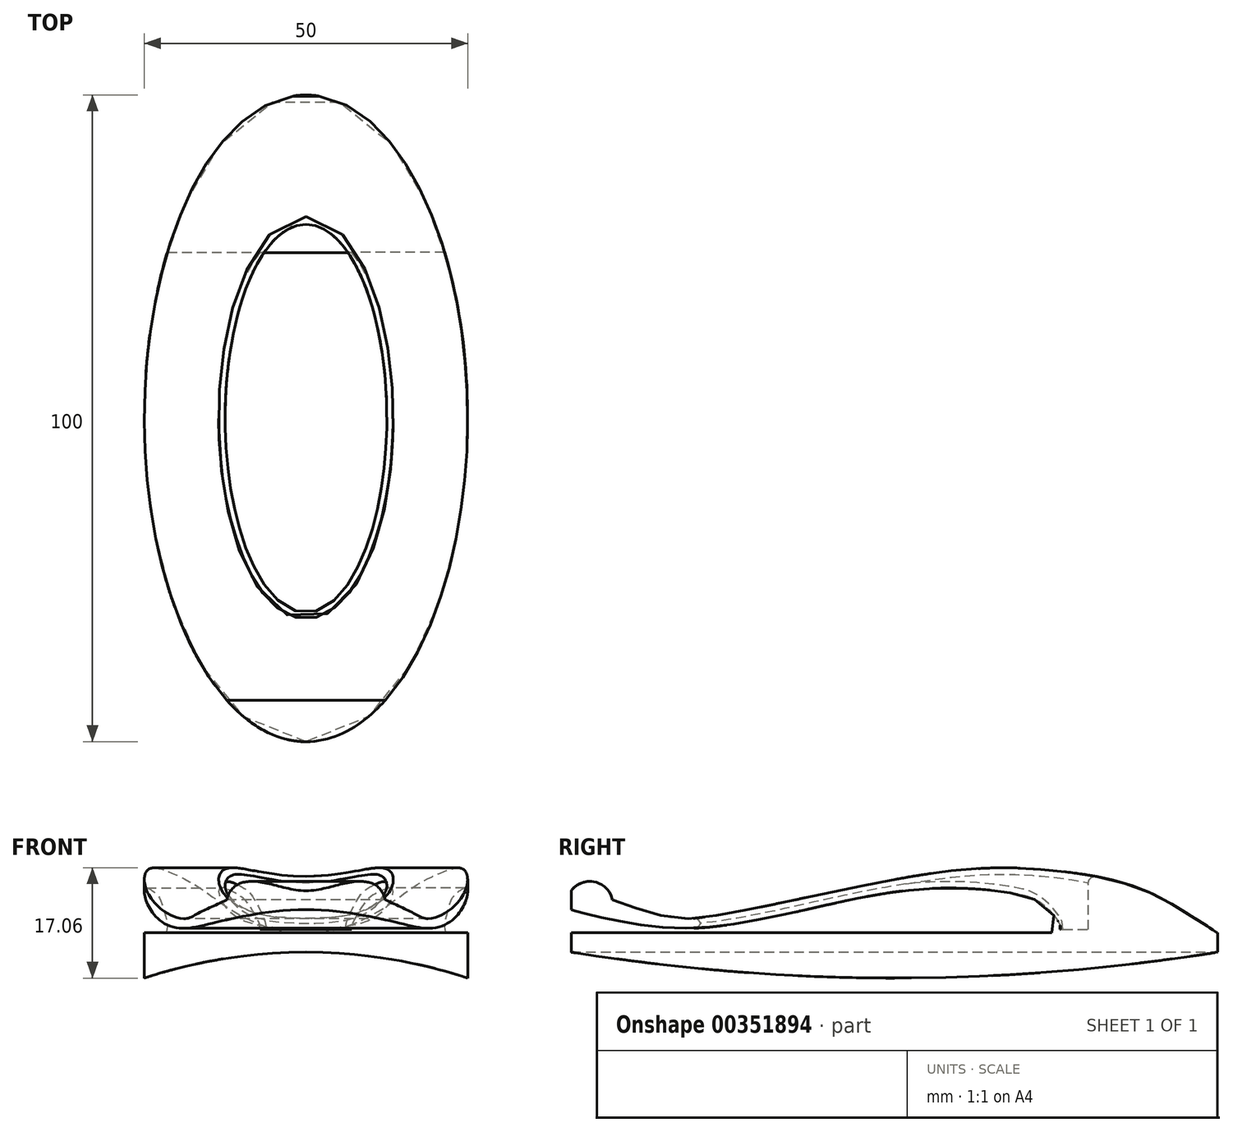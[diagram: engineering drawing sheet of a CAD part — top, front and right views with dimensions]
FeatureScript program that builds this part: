
annotation { "Feature Type Name" : "Feature", "Feature Type Description" : "" }
export const myFeature = defineFeature(function(context is Context, id is Id, definition is map)
    precondition{}
    {
        {
            assignVariable(context, id + "F0", {"name" : "baseWidth", "anyValue" : 50});
        }
        {
            var Q0;
            Q0=qCreatedBy(makeId("Top.planeOp"),FACE);
            var sketch = newSketch(context, id + "F1", { "sketchPlane" : qUnion([Q0])});
            skLineSegment(sketch, "E0.bottom", {"start": v(-25, 50) * mm, "end": v(25, 50) * mm});
            skLineSegment(sketch, "E0.top", {"start": v(-25, -50) * mm, "end": v(25, -50) * mm});
            skLineSegment(sketch, "E0.left", {"start": v(-25, 50) * mm, "end": v(-25, -50) * mm});
            skLineSegment(sketch, "E0.right", {"start": v(25, 50) * mm, "end": v(25, -50) * mm});
            skPoint(sketch, "E0.middle", {"position": v(0, 0) * mm});
            skSolve(sketch);
        }
        {
            var Q0;
            Q0 = qSketchRegion(id + "F1", true);
            extrude(context, id + "F2", {"entities" : qUnion([Q0]), "oppositeDirection" : true, "depth" : 9 * mm});
        }
        {
            var Q0;
            Q0=qCreatedBy(makeId("Front.planeOp"),FACE);
            var sketch = newSketch(context, id + "F3", { "sketchPlane" : qUnion([Q0])});
            skLineSegment(sketch, "E1", {"start": v(0, 0) * mm, "end": v(0, -3) * mm, "construction": true});
            skLineSegment(sketch, "E2", {"start": v(0, -3) * mm, "end": v(0, -83) * mm, "construction": true});
            skPoint(sketch, "E3.MirrorCS.end.orphan", {"position": v(27.63, -4.62) * mm});
            skPoint(sketch, "E3.MirrorCS.start.orphan", {"position": v(0, 0) * mm});
            skPoint(sketch, "E4.MirrorCS.end.orphan", {"position": v(25.3, -9.1) * mm});
            skPoint(sketch, "E5.start.orphan", {"position": v(-27.63, -4.62) * mm});
            skPoint(sketch, "E6.end.orphan", {"position": v(-25.3, -9.1) * mm});
            skPoint(sketch, "E7.MirrorCS.start.orphan", {"position": v(0, -3) * mm});
            skCircle(sketch, "E8", {"center": v(0, -83) * mm, "radius": 80 * mm});
            skSolve(sketch);
        }
        {
            var Q0;
            Q0 = qSketchRegion(id + "F3", true);
            extrude(context, id + "F4", {"entities" : qUnion([Q0]), "operationType" : NewBodyOperationType.REMOVE, "depth" : 58.6 * mm, "hasSecondDirection" : true, "secondDirectionOppositeDirection" : true, "secondDirectionDepth" : 93.1 * mm});
        }
        {
            var Q0;
            Q0=qSketchRegion(id+"F3",true);
            extrude(context, id + "F5", {"entities" : qUnion([Q0]), "operationType" : NewBodyOperationType.REMOVE, "depth" : 59.3 * mm, "hasSecondDirection" : true, "secondDirectionOppositeDirection" : true, "secondDirectionDepth" : 67.2 * mm});
        }
        {
            var Q0;
            Q0=qCreatedBy(makeId("Right.planeOp"),FACE);
            var sketch = newSketch(context, id + "F6", { "sketchPlane" : qUnion([Q0])});
            skLineSegment(sketch, "E9", {"start": v(0, 0) * mm, "end": v(70.45, 0) * mm, "construction": true});
            skFitSpline(sketch, "E10", {"points": [v(49.84, 0) * mm, v(45.5, 2.82) * mm, v(37.77, 6.91) * mm, v(25.1, 9.58) * mm, v(4.82, 9.05) * mm, v(-31.53, 2.2) * mm, v(-37.07, 2.96) * mm, v(-43.6, 5.1) * mm], "startDerivative": vector(-43.63, 31.79) * mm, "endDerivative": vector(-64.7, 27.4) * mm});
            skFitSpline(sketch, "E11", {"points": [v(24.33, 0) * mm, v(23.88, 3.52) * mm, v(18.73, 6.05) * mm, v(7.22, 6.9) * mm, v(-8.3, 4.78) * mm, v(-30.23, 0.75) * mm, v(-42.88, 1.88) * mm, v(-50.65, 3.78) * mm], "startDerivative": vector(92.2, 0) * mm, "endDerivative": vector(-63.45, 20.53) * mm});
            skArc(sketch, "E12", {"start": v(-43.6, 5.1) * mm, "mid": v(-47.78, 7.89) * mm, "end": v(-50.65, 3.78) * mm});
            skPoint(sketch, "E12.third.point", {"position": v(-49.52, 7.02) * mm});
            skArc(sketch, "E13", {"start": v(24.33, 0) * mm, "mid": v(37.09, -2.93) * mm, "end": v(49.84, 0) * mm});
            skSolve(sketch);
        }
        {
            var Q0;
            {var subQ1=sQuery(id+"F6.wireOp",EDGE,"E10");Q0=makeQuery(id+"F6.imprint","IMPRINT",FACE,{"disambiguationData":[TD([[makeQuery(id+"F6.imprint","IMPRINT",EDGE,{"derivedFrom":subQ1}),1.0]])]});}
            extrude(context, id + "F7", {"entities" : qUnion([Q0]), "depth" : (getVariable(context, 'baseWidth') / 2) * mm, "hasSecondDirection" : true, "secondDirectionOppositeDirection" : true, "secondDirectionDepth" : (getVariable(context, 'baseWidth') / 2) * mm});
        }
        {
            var Q0;
            Q0=qCreatedBy(makeId("Top.planeOp"),FACE);
            var sketch = newSketch(context, id + "F8", { "sketchPlane" : qUnion([Q0])});
            skEllipse(sketch, "E14", {"center": v(0, 0) * mm, "majorRadius": 30 * mm, "minorRadius": 12.5 * mm, "majorAxis": v(0, 1)});
            skSolve(sketch);
        }
        {
            var Q0;
            Q0=qSketchRegion(id+"F8",true);
            extrude(context, id + "F9", {"entities" : qUnion([Q0]), "operationType" : NewBodyOperationType.REMOVE, "depth" : 23.9 * mm, "hasSecondDirection" : true, "secondDirectionOppositeDirection" : false, "secondDirectionDepth" : 0.5 * mm});
        }
        {
            var Q0;
            Q0=qCreatedBy(makeId("Top.planeOp"),FACE);
            var sketch = newSketch(context, id + "F10", { "sketchPlane" : qUnion([Q0])});
            skEllipse(sketch, "E15", {"center": v(0, 0) * mm, "majorRadius": 50 * mm, "minorRadius": 25 * mm, "majorAxis": v(0, -1)});
            skSolve(sketch);
        }
        {
            var Q0;
            Q0 = qSketchRegion(id + "F10", true);
            extrude(context, id + "F11", {"entities" : qUnion([Q0]), "operationType" : NewBodyOperationType.INTERSECT, "oppositeDirection" : true, "depth" : 25 * mm, "hasSecondDirection" : true, "secondDirectionOppositeDirection" : false, "secondDirectionDepth" : 25 * mm});
        }
        {
            var Q0;
            Q0=makeQuery(id+"F2.opExtrude","SWEPT_BODY",BODY,{"disambiguationData":[OSD([sQuery(id+"F1.wireOp",EDGE,"E0.bottom"),sQuery(id+"F1.wireOp",EDGE,"E0.top"),sQuery(id+"F1.wireOp",EDGE,"E0.left"),sQuery(id+"F1.wireOp",EDGE,"E0.right")])]});
            var Q1;
            Q1=makeQuery(id+"F7.opExtrude","SWEPT_BODY",BODY,{"disambiguationData":[OSD([sQuery(id+"F6.wireOp",EDGE,"E10"),sQuery(id+"F6.wireOp",EDGE,"E11"),sQuery(id+"F6.wireOp",EDGE,"E12"),sQuery(id+"F6.wireOp",EDGE,"E13")])]});
            booleanBodies(context, id + "F12", {"operationType" : BooleanOperationType.UNION, "tools" : qUnion([Q0, Q1])});
        }
        {
            var Q0;
            Q0=makeQuery(id+"F11.boolean.opBoolean","INTERSECT",EDGE,{"disambiguationData":[OD(1.0)],"derivedFrom":[makeQuery(id+"F7.opExtrude","SWEPT_FACE",FACE,{"disambiguationData":[OSD([sQuery(id+"F6.wireOp",EDGE,"E10")])]}),makeQuery(id+"F11.boolean.toolComplement.opBoolean","COPY",FACE,{"derivedFrom":makeQuery(id+"F11.opExtrude","SWEPT_FACE",FACE,{"disambiguationData":[OSD([sQuery(id+"F10.wireOp",EDGE,"E15")])]})})]});
            var Q1;
            Q1=makeQuery(id+"F9.boolean.opBoolean","INTERSECT",EDGE,{"derivedFrom":[makeQuery(id+"F7.opExtrude","SWEPT_FACE",FACE,{"disambiguationData":[OSD([sQuery(id+"F6.wireOp",EDGE,"E10")])]}),makeQuery(id+"F9.opExtrude","SWEPT_FACE",FACE,{"disambiguationData":[OSD([sQuery(id+"F8.wireOp",EDGE,"E14")])]})]});
            var Q2;
            Q2=makeQuery(id+"F11.boolean.opBoolean","INTERSECT",EDGE,{"derivedFrom":[makeQuery(id+"F7.opExtrude","SWEPT_FACE",FACE,{"disambiguationData":[OSD([sQuery(id+"F6.wireOp",EDGE,"E12")])]}),makeQuery(id+"F11.boolean.toolComplement.opBoolean","COPY",FACE,{"derivedFrom":makeQuery(id+"F11.opExtrude","SWEPT_FACE",FACE,{"disambiguationData":[OSD([sQuery(id+"F10.wireOp",EDGE,"E15")])]})})]});
            var Q3;
            {var subQ0=sQuery(id+"F1.wireOp",EDGE,"E0.right");var subQ1=sQuery(id+"F1.wireOp",EDGE,"E0.left");var subQ2=sQuery(id+"F1.wireOp",EDGE,"E0.top");var subQ3=sQuery(id+"F1.wireOp",EDGE,"E0.bottom");var subQ4=makeQuery(id+"F2.opExtrude","CAP_FACE",FACE,{"disambiguationData":[OSD([subQ3,subQ2,subQ1,subQ0])],"isStart":true});var subQ5=makeQuery(id+"F7.opExtrude","SWEPT_FACE",FACE,{"disambiguationData":[OSD([sQuery(id+"F6.wireOp",EDGE,"E11")])]});var subQ6=makeQuery(id+"F11.boolean.toolComplement.opBoolean","COPY",FACE,{"derivedFrom":makeQuery(id+"F11.opExtrude","SWEPT_FACE",FACE,{"disambiguationData":[OSD([sQuery(id+"F10.wireOp",EDGE,"E15")])]})});Q3=makeQuery(id+"F12.opBoolean","SPLIT",EDGE,{"disambiguationData":[TD([subQ5])],"derivedFrom":makeQuery(id+"F11.boolean.opBoolean","INTERSECT",EDGE,{"derivedFrom":[subQ4,subQ6]})});}
            var Q4;
            Q4=makeQuery(id+"F9.boolean.opBoolean","INTERSECT",EDGE,{"derivedFrom":[makeQuery(id+"F7.opExtrude","SWEPT_FACE",FACE,{"disambiguationData":[OSD([sQuery(id+"F6.wireOp",EDGE,"E11")])]}),makeQuery(id+"F9.opExtrude","SWEPT_FACE",FACE,{"disambiguationData":[OSD([sQuery(id+"F8.wireOp",EDGE,"E14")])]})]});
            var Q5;
            Q5=makeQuery(id+"F11.boolean.opBoolean","INTERSECT",EDGE,{"derivedFrom":[makeQuery(id+"F4.boolean.opBoolean","COPY",FACE,{"derivedFrom":makeQuery(id+"F4.opExtrude","SWEPT_FACE",FACE,{"disambiguationData":[OSD([sQuery(id+"F3.wireOp",EDGE,"E8")])]})}),makeQuery(id+"F11.boolean.toolComplement.opBoolean","COPY",FACE,{"derivedFrom":makeQuery(id+"F11.opExtrude","SWEPT_FACE",FACE,{"disambiguationData":[OSD([sQuery(id+"F10.wireOp",EDGE,"E15")])]})})]});
            fillet(context, id + "F13", {"entities" : qUnion([Q0, Q1, Q2, Q3, Q4, Q5]), "radius" : 1 * mm, "tangentPropagation" : true, "allowEdgeOverflow" : false});
        }
    });
